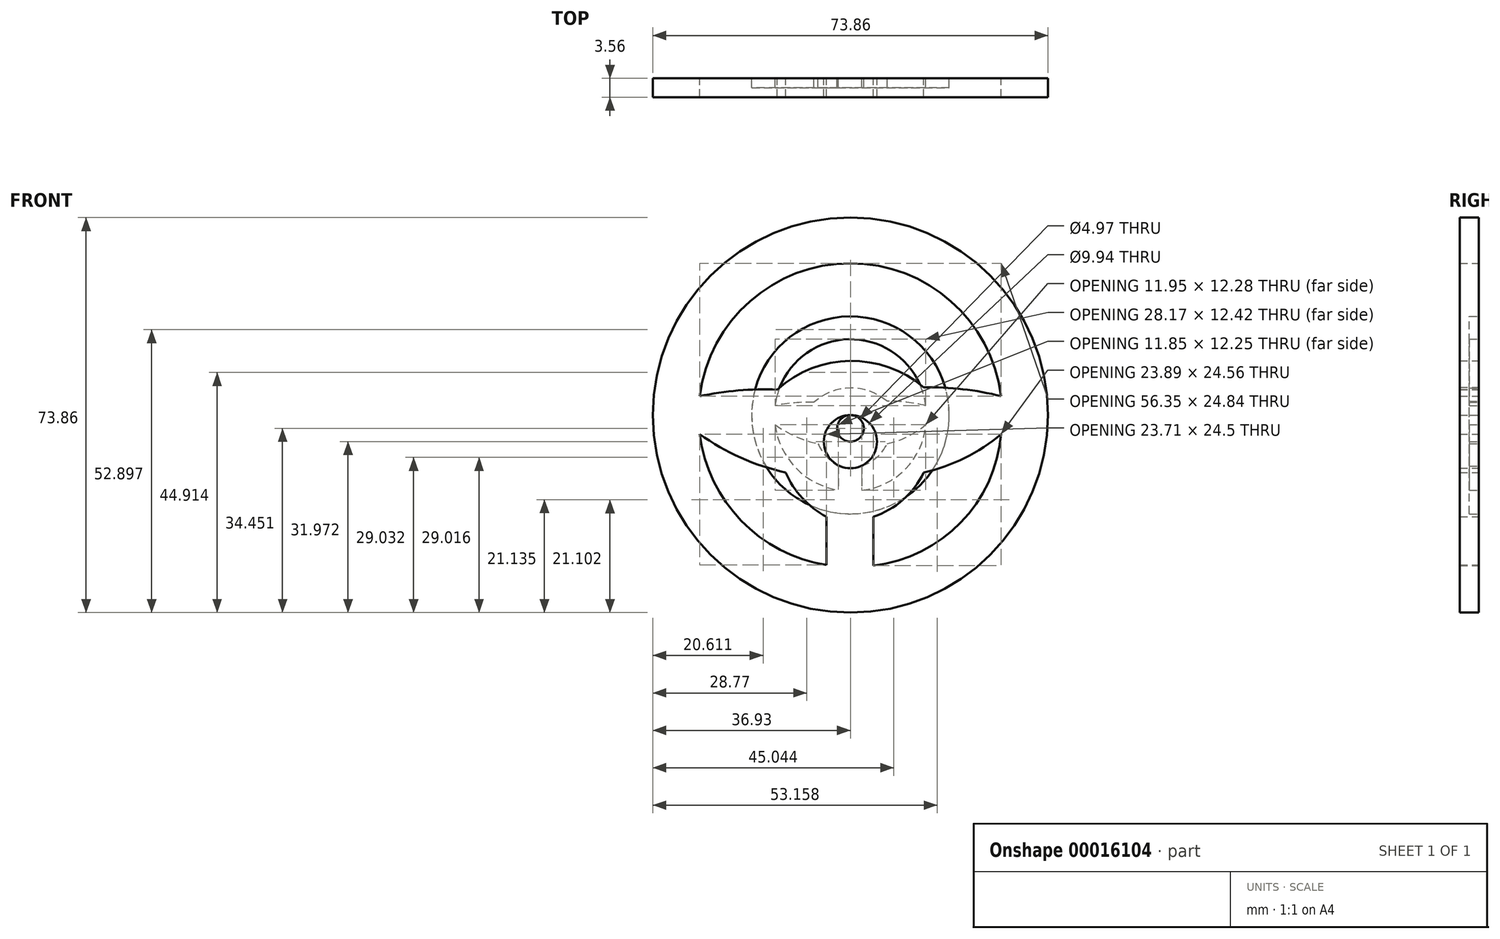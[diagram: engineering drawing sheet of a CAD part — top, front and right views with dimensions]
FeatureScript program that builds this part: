
annotation { "Feature Type Name" : "Feature", "Feature Type Description" : "" }
export const myFeature = defineFeature(function(context is Context, id is Id, definition is map)
    precondition{}
    {
        {
            var Q0;
            Q0=qCreatedBy(makeId("Front.planeOp"),FACE);
            var sketch = newSketch(context, id + "F0", { "sketchPlane" : qUnion([Q0])});
            skCircle(sketch, "E0", {"center": v(0, 0) * mm, "radius": 36.93 * mm});
            skPoint(sketch, "E1", {"position": v(-28.17, -3.55) * mm});
            skPoint(sketch, "E2", {"position": v(-28.17, 3.55) * mm});
            skPoint(sketch, "E3", {"position": v(28.17, 3.55) * mm});
            skArc(sketch, "E4", {"start": v(13.7, 5.21) * mm, "mid": v(-0.07, 10.12) * mm, "end": v(-13.68, 4.77) * mm});
            skLineSegment(sketch, "E5", {"start": v(-4.46, -19) * mm, "end": v(-4.46, -28.04) * mm});
            skArc(sketch, "E6", {"start": v(-28.17, -3.55) * mm, "mid": v(-20.51, -7.96) * mm, "end": v(-12.12, -10.72) * mm});
            skArc(sketch, "E7", {"start": v(-13.68, 4.77) * mm, "mid": v(-20.97, 4.6) * mm, "end": v(-28.17, 3.55) * mm});
            skArc(sketch, "E8", {"start": v(28.17, 3.55) * mm, "mid": v(21, 4.85) * mm, "end": v(13.7, 5.21) * mm});
            skArc(sketch, "E9", {"start": v(-12.12, -10.72) * mm, "mid": v(-8.99, -15.5) * mm, "end": v(-4.46, -19) * mm});
            skArc(sketch, "E10", {"start": v(-28.17, -3.55) * mm, "mid": v(-20.4, -19.75) * mm, "end": v(-4.46, -28.04) * mm});
            skArc(sketch, "E11", {"start": v(28.17, 3.55) * mm, "mid": v(0, 28.39) * mm, "end": v(-28.17, 3.55) * mm});
            skLineSegment(sketch, "E12", {"start": v(4.28, -19) * mm, "end": v(4.28, -28.1) * mm});
            skArc(sketch, "E13", {"start": v(4.28, -19) * mm, "mid": v(9.83, -15.82) * mm, "end": v(13.7, -10.72) * mm});
            skArc(sketch, "E14", {"start": v(13.7, -10.72) * mm, "mid": v(21.37, -8) * mm, "end": v(28.17, -3.55) * mm});
            skArc(sketch, "E15", {"start": v(4.28, -28.1) * mm, "mid": v(20.61, -20.1) * mm, "end": v(28.17, -3.55) * mm});
            skCircle(sketch, "E16", {"center": v(0, -4.96) * mm, "radius": 4.97 * mm});
            skSolve(sketch);
        }
        {
            var Q0;
            Q0=makeQuery(id+"F0.imprint","IMPRINT",FACE,{"disambiguationData":[TD([[makeQuery(id+"F0.imprint","IMPRINT",EDGE,{"derivedFrom":sQuery(id+"F0.wireOp",EDGE,"E0")}),1.0]])]});
            extrude(context, id + "F1", {"entities" : qUnion([Q0]), "depth" : 3.56 * mm});
        }
        {
            var Q0;
            Q0=makeQuery(id+"F1.opExtrude","SWEPT_BODY",BODY,{"disambiguationData":[OSD([sQuery(id+"F0.wireOp",EDGE,"E0"),sQuery(id+"F0.wireOp",EDGE,"E4"),sQuery(id+"F0.wireOp",EDGE,"E5"),sQuery(id+"F0.wireOp",EDGE,"E6"),sQuery(id+"F0.wireOp",EDGE,"E7"),sQuery(id+"F0.wireOp",EDGE,"E8"),sQuery(id+"F0.wireOp",EDGE,"E9"),sQuery(id+"F0.wireOp",EDGE,"E10"),sQuery(id+"F0.wireOp",EDGE,"E11"),sQuery(id+"F0.wireOp",EDGE,"E12"),sQuery(id+"F0.wireOp",EDGE,"E13"),sQuery(id+"F0.wireOp",EDGE,"E14"),sQuery(id+"F0.wireOp",EDGE,"E15"),sQuery(id+"F0.wireOp",EDGE,"E16")])]});
            var Q1;
            Q1=qCreatedBy(makeId("Origin.pointOp"),VERTEX);
            transform(context, id + "F2", {"entities" : qUnion([Q0]), "transformType" : TransformType.SCALE_UNIFORMLY, "scale" : 0.5, "makeCopy" : true, "scalePoint" : qUnion([Q1])});
        }
    });
